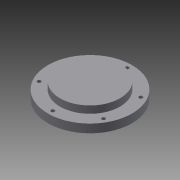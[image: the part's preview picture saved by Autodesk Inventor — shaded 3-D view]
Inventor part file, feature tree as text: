
AUTODESK INVENTOR PART (.ipt)
format: ipt  version: 2015 (Build 190159000, 159)  size: 106,496 bytes
history: native  units: in
note: dims shown in document units (in); Inventor stores cm internally (conversion verified against a paired STEP export)
features: sketch x3, extrude x2, hole x1
ambient origin geometry x8: Origin, YZ Plane, XZ Plane, XY Plane, X Axis, Y Axis, Z Axis, Center Point
bodies: Solid1 (feature_tree)
feature tree (6):
  sketch  "Sketch1"  dims[d1=2.7559in d2=1.9685in]
  sketch  "Sketch2"  dims[d3=1.9685in d4=2.7559in]
  extrude  "Extrusion1"  Depth=1.9685in
  extrude  "Extrusion2"  Depth=2.7559in
  hole  "Hole1"  [1 undecoded]
  sketch  "Sketch3"  dims[d5=0.2756in d6=0.0in d7=0.5118in d8=0.0in d9=0.1575in d10=0.1575in d11=0.1575in d12=0.1575in d13=0.1575in d14=0.1181in d15=0.2362in d16=0.1575in d17=0.0787in d18=90.0deg d19=0.315in d20=0.8108in]
note: 1 required parameter value undecoded (feature->parameter linkage not recoverable at this tier; creation-order binding heuristic only, values carry confidence <= 0.55)
